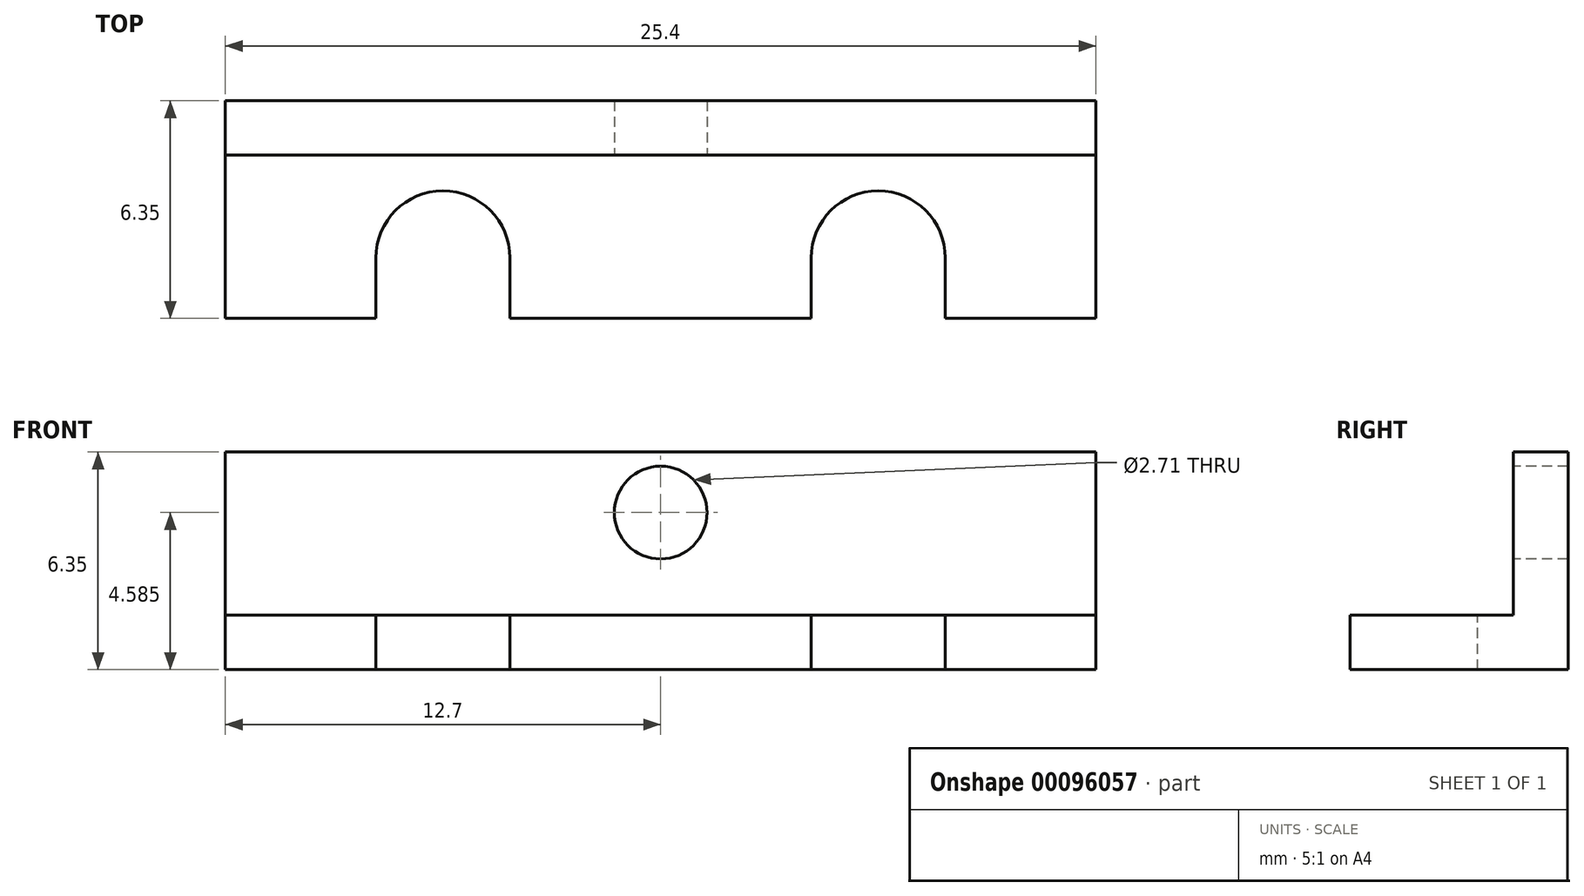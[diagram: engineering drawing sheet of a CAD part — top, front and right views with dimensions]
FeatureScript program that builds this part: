
annotation { "Feature Type Name" : "Feature", "Feature Type Description" : "" }
export const myFeature = defineFeature(function(context is Context, id is Id, definition is map)
    precondition{}
    {
        {
            var Q0;
            Q0=qCreatedBy(makeId("Right.planeOp"),FACE);
            var sketch = newSketch(context, id + "F0", { "sketchPlane" : qUnion([Q0])});
            skLineSegment(sketch, "E0", {"start": v(-6.35, 0) * mm, "end": v(0, 0) * mm});
            skLineSegment(sketch, "E1", {"start": v(0, 0) * mm, "end": v(0, 6.35) * mm});
            skLineSegment(sketch, "E2", {"start": v(0, 6.35) * mm, "end": v(-1.59, 6.35) * mm});
            skLineSegment(sketch, "E3", {"start": v(-1.59, 6.35) * mm, "end": v(-1.59, 1.59) * mm});
            skLineSegment(sketch, "E4", {"start": v(-1.59, 1.59) * mm, "end": v(-6.35, 1.59) * mm});
            skLineSegment(sketch, "E5", {"start": v(-6.35, 1.59) * mm, "end": v(-6.35, 0) * mm});
            skSolve(sketch);
        }
        {
            var Q0;
            Q0 = qSketchRegion(id + "F0", true);
            extrude(context, id + "F1", {"entities" : qUnion([Q0]), "depth" : 25.4 * mm});
        }
        {
            var Q0;
            Q0=makeQuery(id+"F1.opExtrude","SWEPT_FACE",FACE,{"disambiguationData":[OSD([sQuery(id+"F0.wireOp",EDGE,"E4")])]});
            var sketch = newSketch(context, id + "F2", { "sketchPlane" : qUnion([Q0])});
            skArc(sketch, "E6", {"start": v(8.3, -4.58) * mm, "mid": v(6.35, -2.63) * mm, "end": v(4.4, -4.58) * mm});
            skCircle(sketch, "E7", {"center": v(6.35, -4.58) * mm, "radius": 3 * mm, "construction": true});
            skLineSegment(sketch, "E8", {"start": v(4.4, -4.58) * mm, "end": v(4.4, -6.35) * mm});
            skLineSegment(sketch, "E9", {"start": v(8.3, -6.35) * mm, "end": v(8.3, -4.58) * mm});
            skLineSegment(sketch, "E10", {"start": v(4.4, -6.35) * mm, "end": v(8.3, -6.35) * mm});
            skLineSegment(sketch, "E11", {"start": v(12.7, 0) * mm, "end": v(12.7, -6.35) * mm, "construction": true});
            skPoint(sketch, "E11.startSnap0", {"position": v(12.7, -1.59) * mm});
            skArc(sketch, "E12.MirrorCS", {"start": v(17.1, -4.58) * mm, "mid": v(19.05, -2.63) * mm, "end": v(21, -4.58) * mm});
            skLineSegment(sketch, "E13.MirrorCS", {"start": v(17.1, -6.35) * mm, "end": v(17.1, -4.58) * mm});
            skLineSegment(sketch, "E14.MirrorCS", {"start": v(21, -6.35) * mm, "end": v(17.1, -6.35) * mm});
            skLineSegment(sketch, "E15.MirrorCS", {"start": v(21, -4.58) * mm, "end": v(21, -6.35) * mm});
            skSolve(sketch);
        }
        {
            var Q0;
            Q0 = qSketchRegion(id + "F2", true);
            extrude(context, id + "F3", {"entities" : qUnion([Q0]), "operationType" : NewBodyOperationType.REMOVE, "endBound" : BoundingType.THROUGH_ALL, "oppositeDirection" : true, "depth" : 25.4 * mm});
        }
        {
            var Q0;
            Q0=makeQuery(id+"F1.opExtrude","SWEPT_FACE",FACE,{"disambiguationData":[OSD([sQuery(id+"F0.wireOp",EDGE,"E3")])]});
            var sketch = newSketch(context, id + "F4", { "sketchPlane" : qUnion([Q0])});
            skArc(sketch, "E16", {"start": v(10.8, 4.58) * mm, "mid": v(12.7, 2.69) * mm, "end": v(14.6, 4.58) * mm, "construction": true});
            skCircle(sketch, "E17", {"center": v(12.7, 4.58) * mm, "radius": 3 * mm, "construction": true});
            skLineSegment(sketch, "E18", {"start": v(12.7, 6.35) * mm, "end": v(12.7, 4.58) * mm, "construction": true});
            skLineSegment(sketch, "E19", {"start": v(14.6, 4.58) * mm, "end": v(14.6, 6.35) * mm, "construction": true});
            skLineSegment(sketch, "E20", {"start": v(14.6, 6.35) * mm, "end": v(10.8, 6.35) * mm, "construction": true});
            skLineSegment(sketch, "E21", {"start": v(10.8, 6.35) * mm, "end": v(10.8, 4.58) * mm, "construction": true});
            skCircle(sketch, "E22", {"center": v(12.7, 4.58) * mm, "radius": 1.35 * mm});
            skSolve(sketch);
        }
        {
            var Q0;
            Q0 = qSketchRegion(id + "F4", true);
            extrude(context, id + "F5", {"entities" : qUnion([Q0]), "operationType" : NewBodyOperationType.REMOVE, "endBound" : BoundingType.THROUGH_ALL, "oppositeDirection" : true, "depth" : 25.4 * mm});
        }
    });
